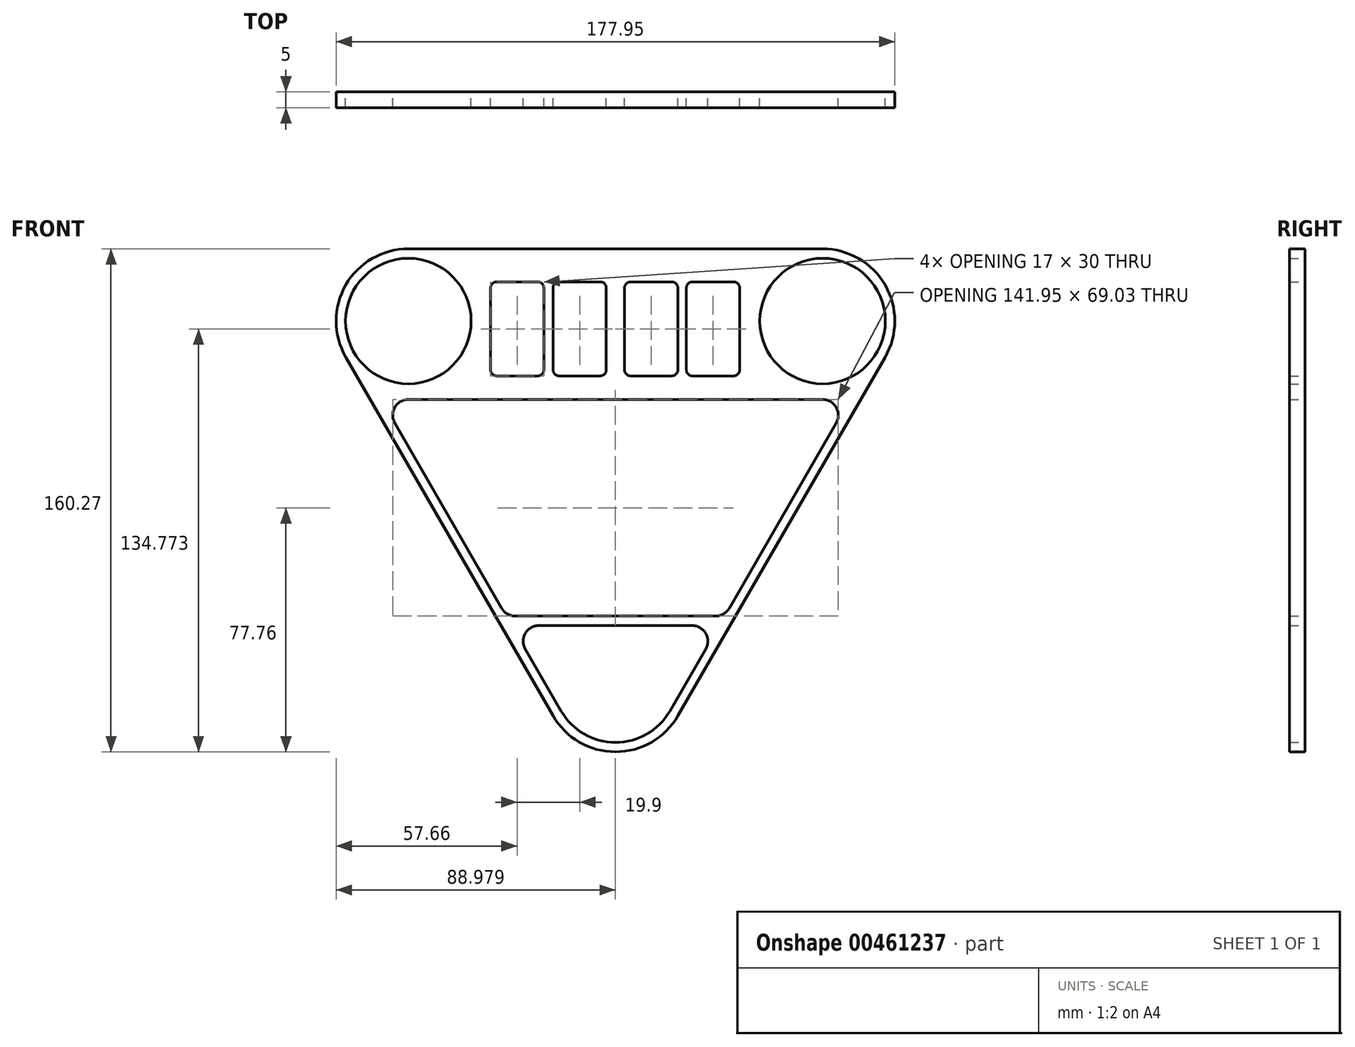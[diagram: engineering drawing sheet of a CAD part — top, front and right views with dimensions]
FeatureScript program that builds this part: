
annotation { "Feature Type Name" : "Feature", "Feature Type Description" : "" }
export const myFeature = defineFeature(function(context is Context, id is Id, definition is map)
    precondition{}
    {
        {
            var Q0;
            Q0=qCreatedBy(makeId("Front.planeOp"),FACE);
            var sketch = newSketch(context, id + "F0", { "sketchPlane" : qUnion([Q0])});
            skLineSegment(sketch, "E0.0", {"start": v(-65.96, 58.2) * mm, "end": v(66, 58.2) * mm});
            skLineSegment(sketch, "E0.1", {"start": v(70.32, 5.7) * mm, "end": v(36.24, -53.33) * mm});
            skLineSegment(sketch, "E0.2", {"start": v(-36.2, -53.33) * mm, "end": v(-70.29, 5.7) * mm});
            skPoint(sketch, "E0.0.midPoint", {"position": v(0, 58.08) * mm});
            skArc(sketch, "E1.filletArc", {"start": v(-65.96, 58.2) * mm, "mid": v(-83.28, 48.2) * mm, "end": v(-83.28, 28.2) * mm});
            skArc(sketch, "E2.filletArc", {"start": v(83.31, 28.2) * mm, "mid": v(83.31, 48.2) * mm, "end": v(66, 58.2) * mm});
            skArc(sketch, "E3.filletArc", {"start": v(-17.3, -86.08) * mm, "mid": v(0.02, -96.08) * mm, "end": v(17.34, -86.08) * mm});
            skArc(sketch, "E4.0", {"start": v(-65.96, 61.2) * mm, "mid": v(-85.87, 49.7) * mm, "end": v(-85.87, 26.7) * mm});
            skArc(sketch, "E4.1", {"start": v(85.91, 26.7) * mm, "mid": v(85.91, 49.7) * mm, "end": v(66, 61.2) * mm});
            skLineSegment(sketch, "E4.2", {"start": v(85.91, 26.7) * mm, "end": v(19.94, -87.58) * mm});
            skLineSegment(sketch, "E4.3", {"start": v(-65.96, 61.2) * mm, "end": v(66, 61.2) * mm});
            skArc(sketch, "E4.4", {"start": v(-19.9, -87.58) * mm, "mid": v(0.02, -99.08) * mm, "end": v(19.94, -87.58) * mm});
            skLineSegment(sketch, "E4.5", {"start": v(-19.9, -87.58) * mm, "end": v(-85.87, 26.7) * mm});
            skCircle(sketch, "E5", {"center": v(-65.96, 38.2) * mm, "radius": 20 * mm});
            skCircle(sketch, "E6", {"center": v(66, 38.2) * mm, "radius": 20 * mm});
            skLineSegment(sketch, "E7", {"start": v(-31.88, -55.83) * mm, "end": v(31.91, -55.83) * mm});
            skLineSegment(sketch, "E8.0", {"start": v(-24.37, -58.83) * mm, "end": v(24.4, -58.83) * mm});
            skCircle(sketch, "E9.0", {"center": v(-65.96, 38.2) * mm, "radius": 17.5 * mm});
            skCircle(sketch, "E10.0", {"center": v(66, 38.2) * mm, "radius": 17.5 * mm});
            skLineSegment(sketch, "E11.bottom", {"start": v(-17.9, 50.7) * mm, "end": v(-4.9, 50.7) * mm});
            skLineSegment(sketch, "E11.top", {"start": v(-17.9, 20.7) * mm, "end": v(-4.9, 20.7) * mm});
            skLineSegment(sketch, "E11.left", {"start": v(-19.9, 48.7) * mm, "end": v(-19.9, 22.7) * mm});
            skLineSegment(sketch, "E11.right", {"start": v(-2.9, 48.7) * mm, "end": v(-2.9, 22.7) * mm});
            skLineSegment(sketch, "E12.bottom", {"start": v(4.9, 50.7) * mm, "end": v(17.9, 50.7) * mm});
            skLineSegment(sketch, "E12.top", {"start": v(4.9, 20.7) * mm, "end": v(17.9, 20.7) * mm});
            skLineSegment(sketch, "E12.left", {"start": v(2.9, 48.7) * mm, "end": v(2.9, 22.7) * mm});
            skLineSegment(sketch, "E12.right", {"start": v(19.9, 48.7) * mm, "end": v(19.9, 22.7) * mm});
            skLineSegment(sketch, "E13.bottom", {"start": v(24.6, 50.7) * mm, "end": v(37.6, 50.7) * mm});
            skLineSegment(sketch, "E13.top", {"start": v(24.6, 20.7) * mm, "end": v(37.6, 20.7) * mm});
            skLineSegment(sketch, "E13.left", {"start": v(22.6, 48.7) * mm, "end": v(22.6, 22.7) * mm});
            skLineSegment(sketch, "E13.right", {"start": v(39.6, 48.7) * mm, "end": v(39.6, 22.7) * mm});
            skPoint(sketch, "E14.end.orphan", {"position": v(0, 20.7) * mm});
            skPoint(sketch, "E15.orphan", {"position": v(-74.81, 0) * mm});
            skLineSegment(sketch, "E16", {"start": v(22.6, 20.7) * mm, "end": v(22.6, 13.2) * mm});
            skLineSegment(sketch, "E17", {"start": v(-65.96, 13.2) * mm, "end": v(66, 13.2) * mm});
            skArc(sketch, "E18.filletArc", {"start": v(-36.2, -53.33) * mm, "mid": v(-34.38, -55.16) * mm, "end": v(-31.88, -55.83) * mm});
            skArc(sketch, "E19.filletArc", {"start": v(31.91, -55.83) * mm, "mid": v(34.41, -55.16) * mm, "end": v(36.24, -53.33) * mm});
            skPoint(sketch, "E20.newPointB", {"position": v(-74.62, 13.2) * mm});
            skArc(sketch, "E20.filletArc", {"start": v(-65.96, 13.2) * mm, "mid": v(-70.29, 10.7) * mm, "end": v(-70.29, 5.7) * mm});
            skArc(sketch, "E21.filletArc", {"start": v(70.32, 5.7) * mm, "mid": v(70.32, 10.7) * mm, "end": v(66, 13.2) * mm});
            skLineSegment(sketch, "E22", {"start": v(-28.7, -66.33) * mm, "end": v(-17.3, -86.08) * mm});
            skLineSegment(sketch, "E23", {"start": v(28.74, -66.33) * mm, "end": v(17.34, -86.08) * mm});
            skPoint(sketch, "E24.visualSharp", {"position": v(-33.03, -58.83) * mm});
            skArc(sketch, "E24.filletArc", {"start": v(-24.37, -58.83) * mm, "mid": v(-28.7, -61.33) * mm, "end": v(-28.7, -66.33) * mm});
            skPoint(sketch, "E25.visualSharp", {"position": v(33.07, -58.83) * mm});
            skArc(sketch, "E25.filletArc", {"start": v(28.74, -66.33) * mm, "mid": v(28.74, -61.33) * mm, "end": v(24.4, -58.83) * mm});
            skPoint(sketch, "E26.visualSharp", {"position": v(-19.9, 50.7) * mm});
            skArc(sketch, "E26.filletArc", {"start": v(-17.9, 50.7) * mm, "mid": v(-19.31, 50.1) * mm, "end": v(-19.9, 48.7) * mm});
            skPoint(sketch, "E27.visualSharp", {"position": v(-2.9, 20.7) * mm});
            skArc(sketch, "E27.filletArc", {"start": v(-4.9, 20.7) * mm, "mid": v(-3.49, 21.28) * mm, "end": v(-2.9, 22.7) * mm});
            skPoint(sketch, "E28.visualSharp", {"position": v(-2.9, 50.7) * mm});
            skArc(sketch, "E28.filletArc", {"start": v(-2.9, 48.7) * mm, "mid": v(-3.49, 50.1) * mm, "end": v(-4.9, 50.7) * mm});
            skPoint(sketch, "E29.visualSharp", {"position": v(-19.9, 20.7) * mm});
            skArc(sketch, "E29.filletArc", {"start": v(-19.9, 22.7) * mm, "mid": v(-19.31, 21.28) * mm, "end": v(-17.9, 20.7) * mm});
            skPoint(sketch, "E30.visualSharp", {"position": v(2.9, 50.7) * mm});
            skArc(sketch, "E30.filletArc", {"start": v(4.9, 50.7) * mm, "mid": v(3.49, 50.1) * mm, "end": v(2.9, 48.7) * mm});
            skPoint(sketch, "E31.visualSharp", {"position": v(2.9, 20.7) * mm});
            skArc(sketch, "E31.filletArc", {"start": v(2.9, 22.7) * mm, "mid": v(3.49, 21.28) * mm, "end": v(4.9, 20.7) * mm});
            skPoint(sketch, "E32.visualSharp", {"position": v(19.9, 20.7) * mm});
            skArc(sketch, "E32.filletArc", {"start": v(17.9, 20.7) * mm, "mid": v(19.31, 21.28) * mm, "end": v(19.9, 22.7) * mm});
            skPoint(sketch, "E33.visualSharp", {"position": v(19.9, 50.7) * mm});
            skArc(sketch, "E33.filletArc", {"start": v(19.9, 48.7) * mm, "mid": v(19.31, 50.1) * mm, "end": v(17.9, 50.7) * mm});
            skPoint(sketch, "E34.visualSharp", {"position": v(22.6, 50.7) * mm});
            skArc(sketch, "E34.filletArc", {"start": v(24.6, 50.7) * mm, "mid": v(23.19, 50.1) * mm, "end": v(22.6, 48.7) * mm});
            skPoint(sketch, "E35.visualSharp", {"position": v(39.6, 50.7) * mm});
            skArc(sketch, "E35.filletArc", {"start": v(39.6, 48.7) * mm, "mid": v(39.01, 50.1) * mm, "end": v(37.6, 50.7) * mm});
            skPoint(sketch, "E36.visualSharp", {"position": v(39.6, 20.7) * mm});
            skArc(sketch, "E36.filletArc", {"start": v(37.6, 20.7) * mm, "mid": v(39.01, 21.28) * mm, "end": v(39.6, 22.7) * mm});
            skPoint(sketch, "E37.visualSharp", {"position": v(22.6, 20.7) * mm});
            skArc(sketch, "E37.filletArc", {"start": v(22.6, 22.7) * mm, "mid": v(23.19, 21.28) * mm, "end": v(24.6, 20.7) * mm});
            skLineSegment(sketch, "E38.bottom", {"start": v(-37.8, 50.7) * mm, "end": v(-24.8, 50.7) * mm});
            skLineSegment(sketch, "E38.top", {"start": v(-37.8, 20.7) * mm, "end": v(-24.8, 20.7) * mm});
            skLineSegment(sketch, "E38.left", {"start": v(-39.8, 48.7) * mm, "end": v(-39.8, 22.7) * mm});
            skLineSegment(sketch, "E38.right", {"start": v(-22.8, 48.7) * mm, "end": v(-22.8, 22.7) * mm});
            skPoint(sketch, "E39.end.orphan", {"position": v(-19.85, 20.7) * mm});
            skPoint(sketch, "E40.visualSharp", {"position": v(-39.8, 50.7) * mm});
            skArc(sketch, "E40.filletArc", {"start": v(-37.8, 50.7) * mm, "mid": v(-39.21, 50.1) * mm, "end": v(-39.8, 48.7) * mm});
            skPoint(sketch, "E41.visualSharp", {"position": v(-22.8, 20.7) * mm});
            skArc(sketch, "E41.filletArc", {"start": v(-24.8, 20.7) * mm, "mid": v(-23.39, 21.28) * mm, "end": v(-22.8, 22.7) * mm});
            skPoint(sketch, "E42.visualSharp", {"position": v(-22.8, 50.7) * mm});
            skArc(sketch, "E42.filletArc", {"start": v(-22.8, 48.7) * mm, "mid": v(-23.39, 50.1) * mm, "end": v(-24.8, 50.7) * mm});
            skPoint(sketch, "E43.visualSharp", {"position": v(-39.8, 20.7) * mm});
            skArc(sketch, "E43.filletArc", {"start": v(-39.8, 22.7) * mm, "mid": v(-39.21, 21.28) * mm, "end": v(-37.8, 20.7) * mm});
            skSolve(sketch);
        }
        {
            var Q0;
            Q0=makeQuery(id+"F0.imprint","IMPRINT",FACE,{"disambiguationData":[TD([[makeQuery(id+"F0.imprint","IMPRINT",EDGE,{"derivedFrom":sQuery(id+"F0.wireOp",EDGE,"E0.1")}),1.0]])]});
            extrude(context, id + "F1", {"entities" : qUnion([Q0]), "endBound" : BoundingType.SYMMETRIC, "depth" : 5 * mm});
        }
    });
